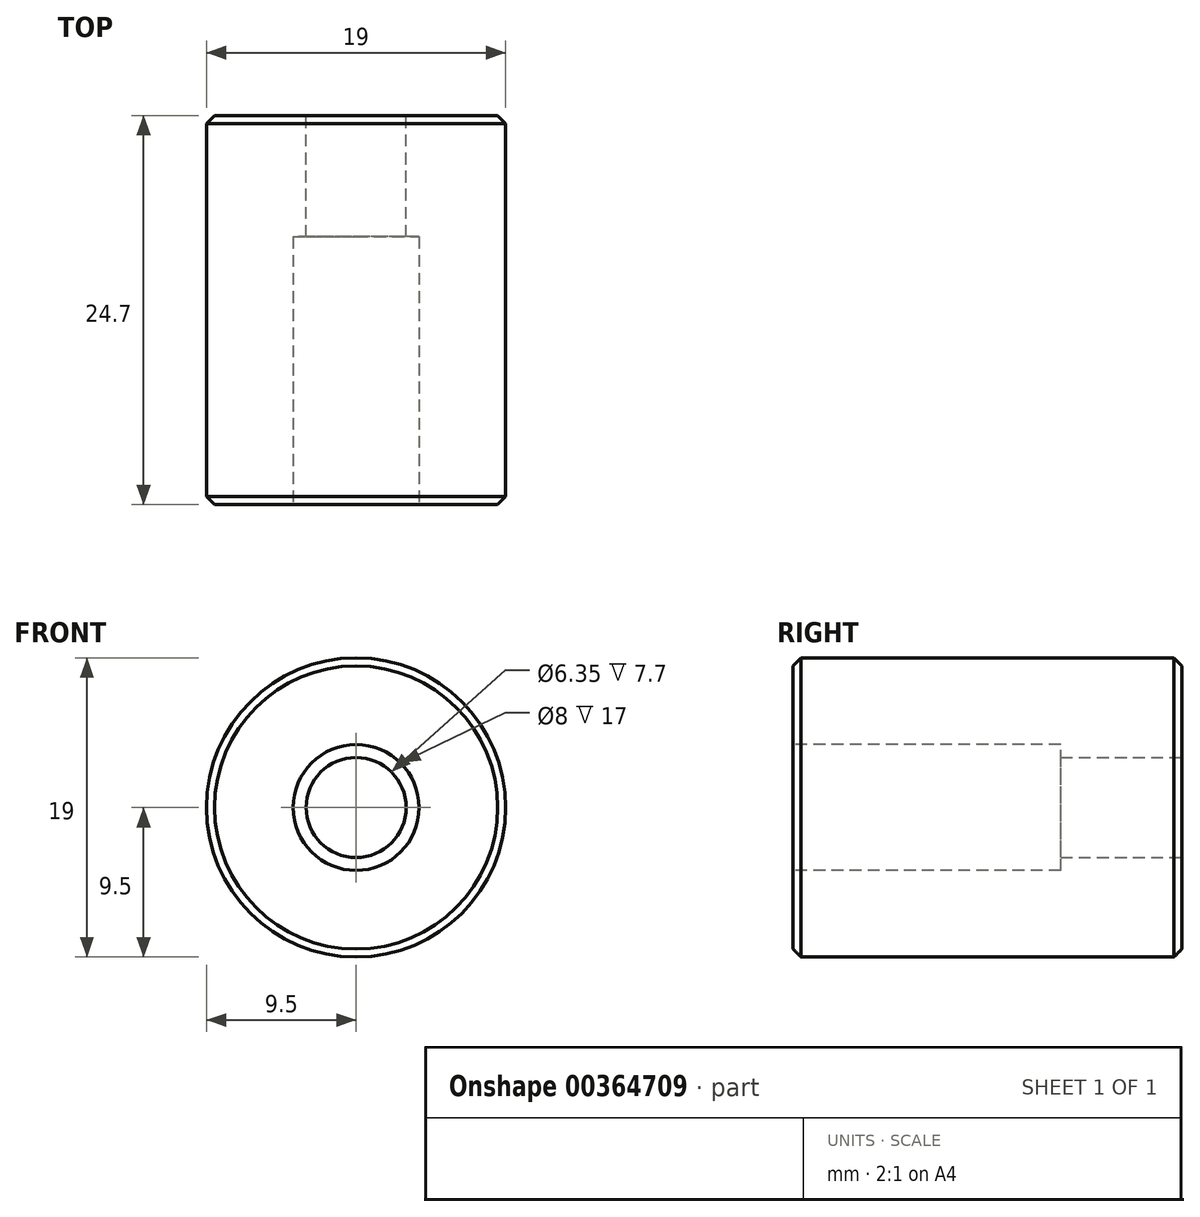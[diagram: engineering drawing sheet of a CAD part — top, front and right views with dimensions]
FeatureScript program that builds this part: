
annotation { "Feature Type Name" : "Feature", "Feature Type Description" : "" }
export const myFeature = defineFeature(function(context is Context, id is Id, definition is map)
    precondition{}
    {
        {
            var Q0;
            Q0=qCreatedBy(makeId("Front.planeOp"),FACE);
            var sketch = newSketch(context, id + "F0", { "sketchPlane" : qUnion([Q0])});
            skCircle(sketch, "E0", {"center": v(0, 0) * mm, "radius": 9.5 * mm});
            skCircle(sketch, "E1", {"center": v(0, 0) * mm, "radius": 3.17 * mm});
            skSolve(sketch);
        }
        {
            var Q0;
            Q0 = qSketchRegion(id + "F0", true);
            extrude(context, id + "F1", {"entities" : qUnion([Q0]), "depth" : 24.7 * mm});
        }
        {
            var Q0;
            Q0=makeQuery(id+"F1.opExtrude","CAP_FACE",FACE,{"disambiguationData":[OSD([sQuery(id+"F0.wireOp",EDGE,"E0"),sQuery(id+"F0.wireOp",EDGE,"E1")])],"isStart":false});
            var sketch = newSketch(context, id + "F2", { "sketchPlane" : qUnion([Q0])});
            skCircle(sketch, "E2", {"center": v(0, 0) * mm, "radius": 4 * mm});
            skSolve(sketch);
        }
        {
            var Q0;
            Q0 = qSketchRegion(id + "F2", true);
            extrude(context, id + "F3", {"entities" : qUnion([Q0]), "operationType" : NewBodyOperationType.REMOVE, "oppositeDirection" : true, "depth" : 17 * mm});
        }
        {
            var Q0;
            Q0=makeQuery(id+"F1.opExtrude","SWEPT_FACE",FACE,{"disambiguationData":[OSD([sQuery(id+"F0.wireOp",EDGE,"E0")])]});
            chamfer(context, id + "F4", {"entities" : qUnion([Q0]), "width" : 0.5 * mm, "tangentPropagation" : true});
        }
    });
